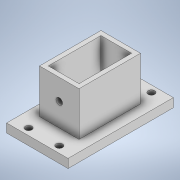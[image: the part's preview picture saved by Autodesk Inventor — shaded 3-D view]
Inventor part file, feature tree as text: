
AUTODESK INVENTOR PART (.ipt)
format: ipt  version: 2022 (Build 260153000, 153)  size: 148,992 bytes
history: native  units: mm
features: extrude x4, sketch x4
ambient origin geometry x8: Origin, YZ Plane, XZ Plane, XY Plane, X Axis, Y Axis, Z Axis, Center Point
bodies: Solid1 (feature_tree)
feature tree (8):
  extrude  "Extrusion1"  Depth=12.0mm
  extrude  "Extrusion3"  Depth=1.0mm
  extrude  "Extrusion5"  Depth=1.75mm
  extrude  "Extrusion6"  Depth=5.0mm TaperAngle=0.0deg
  sketch  "Sketch1"  dims[d0=7.0mm d1=12.0mm]
  sketch  "Sketch3"  dims[d3=1.0mm d4=0.0mm d8=0.75mm]
  sketch  "Sketch7"  dims[d9=0.75mm d10=1.75mm]
  sketch  "Sketch8"  dims[d11=20.0mm d13=3.5mm d14=20.0mm d16=10.5mm d19=5.0mm d20=0.0mm d28=1.75mm d29=1.75mm d30=3.0mm d31=3.0mm d32=0.5mm d33=5.0mm d34=0.0mm d35=0.75mm d36=2.0mm d37=2.25mm d38=0.0mm d39=0.0mm d21=0.5mm d22=0.872665mm d23=0.5mm d24=0.872665mm]
